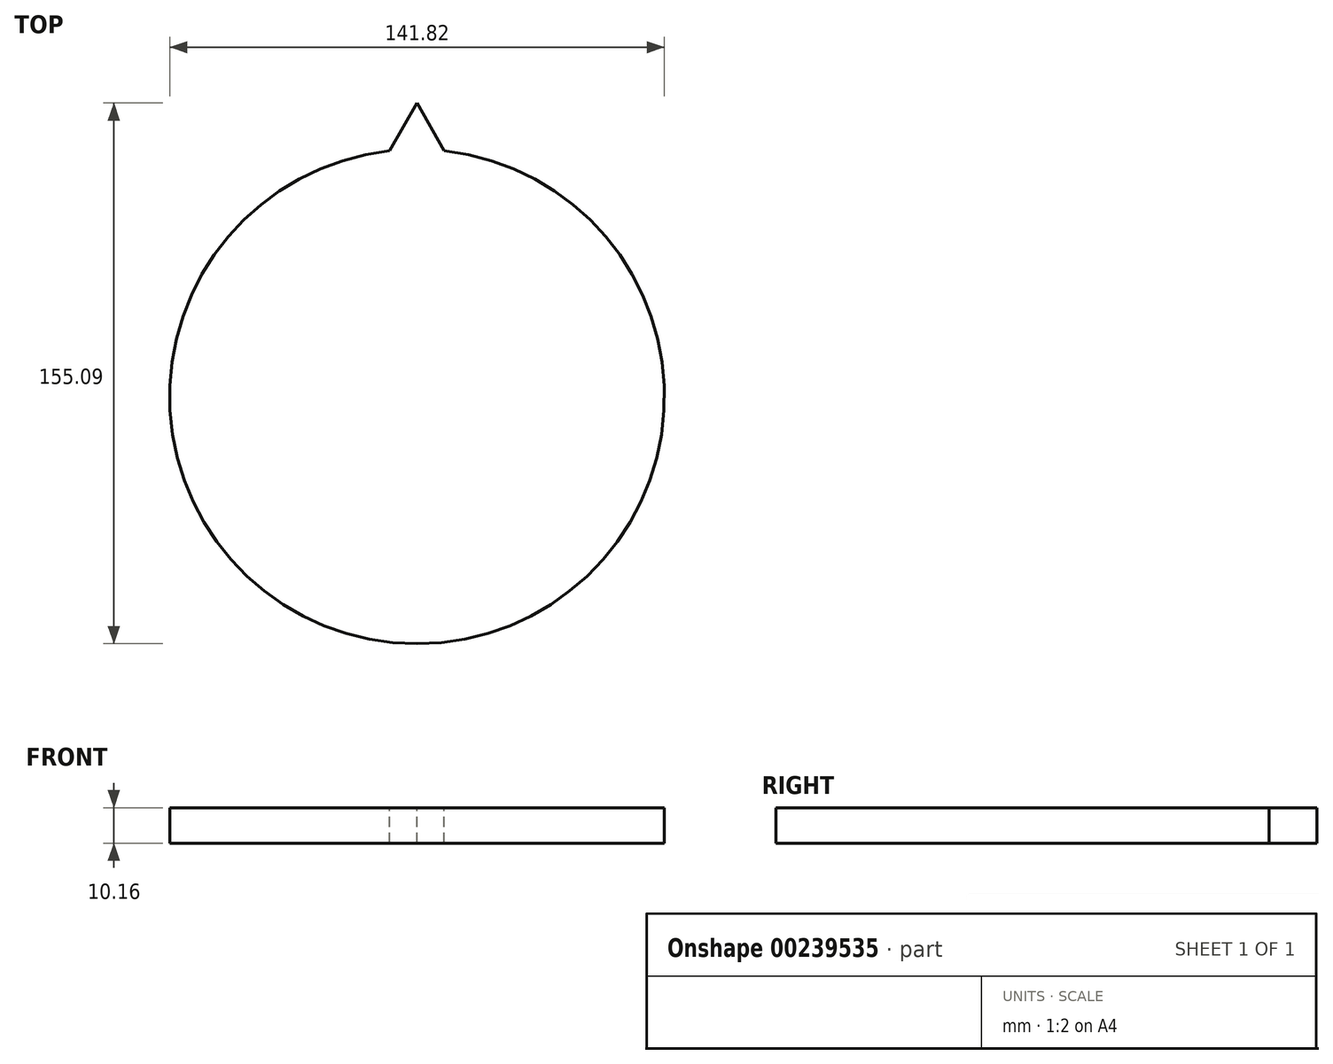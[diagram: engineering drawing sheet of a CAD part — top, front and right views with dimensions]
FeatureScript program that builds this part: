
annotation { "Feature Type Name" : "Feature", "Feature Type Description" : "" }
export const myFeature = defineFeature(function(context is Context, id is Id, definition is map)
    precondition{}
    {
        {
            var Q0;
            Q0=qCreatedBy(makeId("Top.planeOp"),FACE);
            var sketch = newSketch(context, id + "F0", { "sketchPlane" : qUnion([Q0])});
            skCircle(sketch, "E0", {"center": v(0, 0) * mm, "radius": 70.9 * mm});
            skSolve(sketch);
        }
        {
            var Q0;
            Q0 = qSketchRegion(id + "F0", true);
            extrude(context, id + "F1", {"entities" : qUnion([Q0]), "depth" : 10.16 * mm});
        }
        {
            var Q0;
            Q0=makeQuery(id+"F1.opExtrude","CAP_FACE",FACE,{"disambiguationData":[OSD([sQuery(id+"F0.wireOp",EDGE,"E0")])],"isStart":false});
            var sketch = newSketch(context, id + "F2", { "sketchPlane" : qUnion([Q0])});
            skLineSegment(sketch, "E1", {"start": v(-7.83, 70.47) * mm, "end": v(0, 84.18) * mm});
            skLineSegment(sketch, "E2", {"start": v(0, 84.18) * mm, "end": v(7.83, 70.47) * mm});
            skLineSegment(sketch, "E3", {"start": v(7.83, 70.47) * mm, "end": v(-7.83, 70.47) * mm});
            skSolve(sketch);
        }
        {
            var Q0;
            Q0 = qSketchRegion(id + "F2", true);
            extrude(context, id + "F3", {"entities" : qUnion([Q0]), "operationType" : NewBodyOperationType.ADD, "oppositeDirection" : true, "depth" : 10.16 * mm});
        }
    });
